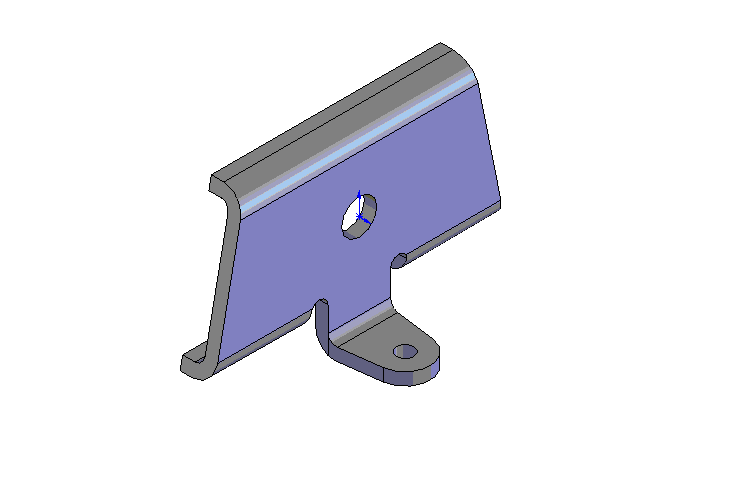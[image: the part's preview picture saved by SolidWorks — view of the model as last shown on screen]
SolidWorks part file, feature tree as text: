
SOLIDWORKS PART (.sldprt)
format: sldprt  version: not decoded by parser v0  size: 434,688 bytes
history: native  units: mm
features: sketch x7, cut_extrude x5, plane x3, extrude x2, fillet x2, material x1 (+10 scaffold rows collapsed)
feature tree (30):
  scaffold x10  (default folders/planes/origin — collapsed)
  material  "Matériau <non spécifié>"
  plane  "Plan de face"
  plane  "Plan de dessus"
  plane  "Plan de droite"
  sketch  "Esquisse1"  dims[c1.D1=3.0mm c1.D2=3.0mm c1.D3=37.0mm c1.D4=60.0mm c1.D5=15.0mm c1.D6=8.0mm c1.D8=43.0mm c1.D9=31.0mm c2.D8=44.0mm c2.D10=20.0mm c2.D11=8.0mm c2.D7=3.0mm]
  extrude  "Extrusion1"  Depth=70mm
  sketch  "Esquisse2"  dims[c1.D3=~1.998824mm c1.D1=~3.997648mm c1.D2=15.0mm c2.D3=31.0mm]
  cut_extrude  "Enlèv. mat.-Extru.1"  [1 undecoded]
  sketch  "Esquisse8"
  cut_extrude  "Enlèv. mat.-Extru.8"  [1 undecoded]
  sketch  "Esquisse9"
  cut_extrude  "Enlèv. mat.-Extru.9"  [1 undecoded]
  sketch  "Esquisse11"  dims[D2=6.0mm D3=4.2mm D1=14.0mm]
  extrude  "Extrusion2"  Depth=3mm
  sketch  "Esquisse12"  dims[D1=8.5mm]
  cut_extrude  "Enlèv. mat.-Extru.10"  [1 undecoded]
  fillet  "Congé3"  Radius=2mm
  fillet  "Congé4"  Radius=5mm
  sketch  "Esquisse13"  dims[D1=55.0mm]
  cut_extrude  "Enlèv. mat.-Extru.11"  [1 undecoded]
decode coverage: 9 of 16 modeling features carry decoded parameters
note: ~ marks probable driven/reference dimensions
note: 5 parameter values undecoded
summary: no parameter record found for 5 features
note: suppression state not decoded; provenance and decode notes live in map.json
